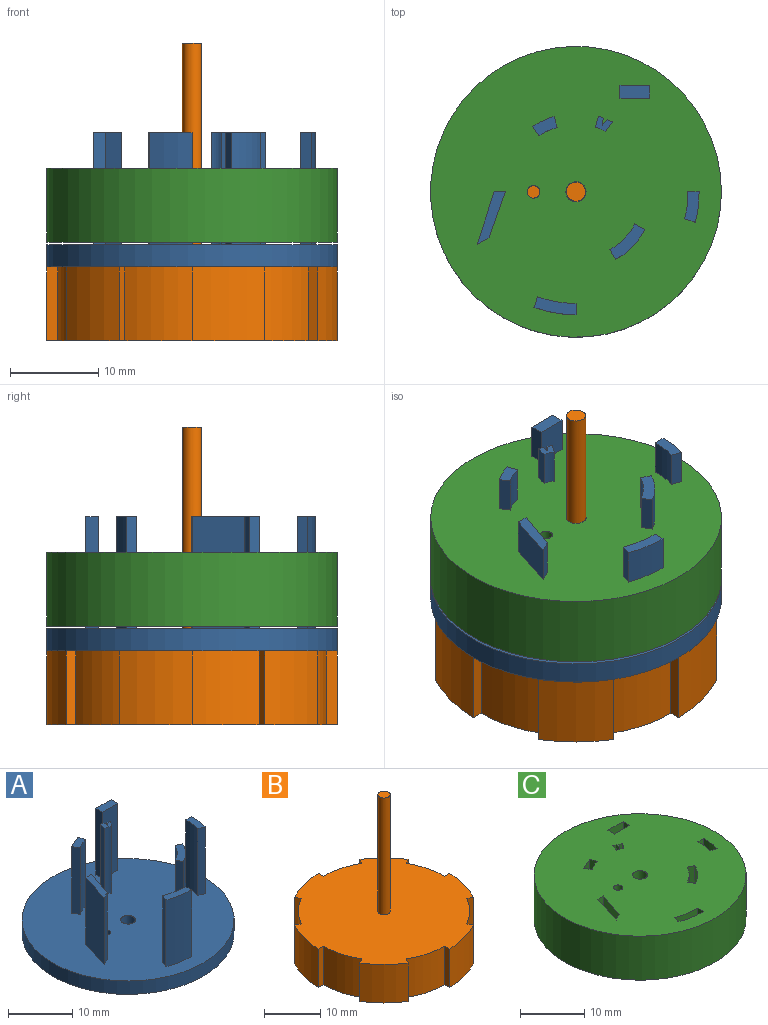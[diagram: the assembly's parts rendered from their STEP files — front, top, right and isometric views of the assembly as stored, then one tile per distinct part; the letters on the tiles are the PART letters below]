
ASSEMBLY  parts=3 mates=2
PART A: 43 faces, bbox 33x33x15.2 mm
  f0: cylinder r=16.51mm len=33.02mm, axis (0,0,-1), area 263.5mm2, adj f3,f4
  f1: cylinder r=0.72mm len=2.54mm, axis (0,0,-1), area 11.4mm2, adj f3,f4
  f2: cylinder r=1.14mm len=2.54mm, axis (0,0,-1), area 18.2mm2, adj f3,f4
  f3: plane 33.02x33.02mm, normal (0,0,1), area 818.2mm2, adj f0,f1,f2,f6,f7,f8,f9,f11
  f4: plane 33.02x33.02mm, normal (0,0,-1), area 850.6mm2, adj f0,f1,f2
  f5: plane 4.78x2.04mm, normal (0,0,1), area 5.9mm2, adj f6,f7,f8,f9
  f6: plane 12.7x1.27mm, normal (1,0,0), area 16.1mm2, adj f3,f5,f7,f9
  f7: cylinder r=14.67mm len=12.7mm, axis (0,0,-1), area 61.9mm2, adj f3,f5,f6,f8
  f8: plane 12.7x1.19mm, normal (-0.94,0.34,0), area 16.1mm2, adj f3,f5,f7,f9
  f9: cylinder r=13.5mm len=12.7mm, axis (0,0,-1), area 56.3mm2, adj f3,f5,f6,f8
  f10: plane 2.82x2.22mm, normal (0,0,1), area 3.2mm2, adj f11,f12,f13,f14
  f11: plane 12.7x1.08mm, normal (-0.83,-0.55,0), area 16.5mm2, adj f3,f10,f12,f14
  f12: cylinder r=10.87mm len=12.7mm, axis (0,0,-1), area 34.5mm2, adj f3,f10,f11,f13
  f13: plane 12.7x1.24mm, normal (0.96,0.28,0), area 16.5mm2, adj f3,f10,f12,f14
  f14: cylinder r=7.47mm len=12.7mm, axis (0,0,-1), area 29.5mm2, adj f3,f10,f11,f13
  f15: plane 4.05x3.98mm, normal (0,0,1), area 5.9mm2, adj f16,f17,f18,f19
  f16: plane 12.7x1.14mm, normal (0.48,0.88,0), area 16.5mm2, adj f3,f15,f17,f19
  f17: cylinder r=7.87mm len=12.7mm, axis (0,0,-1), area 61.6mm2, adj f3,f15,f16,f18
  f18: plane 12.7x1.12mm, normal (-0.86,-0.51,0), area 16.5mm2, adj f3,f15,f17,f19
  f19: cylinder r=6.99mm len=12.7mm, axis (0,0,-1), area 52.6mm2, adj f3,f15,f16,f18
  f20: plane 3.47x1.65mm, normal (0,0,1), area 4.2mm2, adj f21,f22,f23,f24
  f21: plane 12.7x1.27mm, normal (0,1,0), area 16.1mm2, adj f3,f20,f22,f24
  f22: cylinder r=11.39mm len=12.7mm, axis (0,0,-1), area 44.6mm2, adj f3,f20,f21,f23
  f23: plane 12.7x1.21mm, normal (-0.32,-0.95,0), area 16.2mm2, adj f3,f20,f22,f24
  f24: cylinder r=9.62mm len=12.7mm, axis (0,0,-1), area 39.3mm2, adj f3,f20,f21,f23
  f25: plane 5.96x3.21mm, normal (0,0,1), area 6.6mm2, adj f26,f27,f28,f29
  f26: plane 12.7x1.27mm, normal (0,1,0), area 16.1mm2, adj f3,f25,f27,f29
  f27: plane 12.7x5.24mm, normal (0.94,-0.33,0), area 70.6mm2, adj f3,f25,f26,f28
  f28: plane 12.7x1.35mm, normal (0.47,-0.88,0), area 19.4mm2, adj f3,f25,f27,f29
  f29: plane 12.7x5.96mm, normal (-0.95,0.31,0), area 79.5mm2, adj f3,f25,f26,f28
  f30: plane 1.89x1.72mm, normal (0,0,1), area 1.6mm2, adj f31,f32,f33,f34,f35,f36,f37
  f31: plane 12.7x0.85mm, normal (0.99,-0.15,0), area 10.9mm2, adj f3,f30,f32,f37
  f32: plane 12.7x0.68mm, normal (-0.78,0.63,0), area 11.1mm2, adj f3,f30,f31,f33
  f33: plane 12.7x0.57mm, normal (0.43,0.9,0), area 8mm2, adj f3,f30,f32,f34
  f34: plane 12.7x1.06mm, normal (0.81,-0.59,0), area 16.7mm2, adj f3,f30,f33,f35
  f35: cylinder r=2.37mm len=12.7mm, axis (0,0,-1), area 15.4mm2, adj f3,f30,f34,f36
  f36: plane 12.7x1.28mm, normal (-0.97,0.25,0), area 16.8mm2, adj f3,f30,f35,f37
  f37: plane 12.7x0.57mm, normal (0.35,0.94,0), area 7.7mm2, adj f3,f30,f31,f36
  f38: plane 3.35x1.47mm, normal (0,0,1), area 4.9mm2, adj f39,f40,f41,f42
  f39: plane 12.7x1.47mm, normal (1,0,0), area 18.7mm2, adj f3,f38,f40,f42
  f40: plane 12.7x3.35mm, normal (0,-1,0), area 42.6mm2, adj f3,f38,f39,f41
  f41: plane 12.7x1.47mm, normal (-1,0,0), area 18.7mm2, adj f3,f38,f40,f42
  f42: plane 12.7x3.35mm, normal (0,1,0), area 42.6mm2, adj f3,f38,f39,f41
PART B: 28 faces, bbox 33x33x33.8 mm
  f0: cylinder r=15.24mm len=8.38mm, axis (0,0,-1), area 66.9mm2, adj f5,f6,f10,f24
  f1: cylinder r=15.24mm len=8.38mm, axis (0,0,-1), area 66.9mm2, adj f5,f10,f15,f26
  f2: cylinder r=15.24mm len=8.38mm, axis (0,0,-1), area 66.9mm2, adj f5,f10,f14,f18
  f3: cylinder r=15.24mm len=8.38mm, axis (0,0,-1), area 66.9mm2, adj f5,f10,f21,f23
  f4: cylinder r=15.24mm len=8.38mm, axis (0,0,-1), area 66.9mm2, adj f5,f10,f17,f20
  f5: plane 33.02x33.02mm, normal (0,0,1), area 786.3mm2, adj f0,f1,f2,f3,f4,f6,f7,f8
  f6: plane 8.38x1.1mm, normal (-0.87,-0.5,0), area 10.6mm2, adj f0,f5,f9,f10
  f7: cylinder r=15.24mm len=8.38mm, axis (0,0,-1), area 66.9mm2, adj f5,f8,f10,f25
  f8: plane 8.38x1.27mm, normal (1,0,0), area 10.6mm2, adj f5,f7,f9,f10
  f9: cylinder r=19.46mm len=8.38mm, axis (0,0,-1), area 72.2mm2, adj f5,f6,f8,f10
  f10: plane 33.02x33.02mm, normal (0,0,-1), area 790mm2, adj f0,f1,f2,f3,f4,f6,f7,f8
  f11: plane 2.17x2.17mm, normal (0,0,1), area 3.7mm2, adj f12
  f12: cylinder r=1.08mm len=25.4mm, axis (0,0,-1), area 173mm2, adj f5,f11
  f13: cylinder r=19.46mm len=8.38mm, axis (0,0,-1), area 72.2mm2, adj f5,f10,f14,f15
  f14: plane 8.38x1.1mm, normal (-0.5,-0.87,0), area 10.6mm2, adj f2,f5,f10,f13
  f15: plane 8.38x1.27mm, normal (0,1,0), area 10.6mm2, adj f1,f5,f10,f13
  f16: cylinder r=19.46mm len=8.38mm, axis (0,0,-1), area 72.2mm2, adj f5,f10,f17,f18
  f17: plane 8.38x1.27mm, normal (-1,0,0), area 10.6mm2, adj f4,f5,f10,f16
  f18: plane 8.38x1.1mm, normal (0.87,0.5,0), area 10.6mm2, adj f2,f5,f10,f16
  f19: cylinder r=19.46mm len=8.38mm, axis (0,0,-1), area 72.2mm2, adj f5,f10,f20,f21
  f20: plane 8.38x1.1mm, normal (0.87,-0.5,0), area 10.6mm2, adj f4,f5,f10,f19
  f21: plane 8.38x1.1mm, normal (-0.5,0.87,0), area 10.6mm2, adj f3,f5,f10,f19
  f22: cylinder r=19.46mm len=8.38mm, axis (0,0,-1), area 72.2mm2, adj f5,f10,f23,f24
  f23: plane 8.38x1.27mm, normal (0,-1,0), area 10.6mm2, adj f3,f5,f10,f22
  f24: plane 8.38x1.1mm, normal (0.5,0.87,0), area 10.6mm2, adj f0,f5,f10,f22
  f25: plane 8.38x1.1mm, normal (-0.87,0.5,0), area 10.6mm2, adj f5,f7,f10,f27
  f26: plane 8.38x1.1mm, normal (0.5,-0.87,0), area 10.6mm2, adj f1,f5,f10,f27
  f27: cylinder r=19.46mm len=8.38mm, axis (0,0,-1), area 72.2mm2, adj f5,f10,f25,f26
PART C: 36 faces, bbox 33x33x8.4 mm
  f0: plane 8.38x1.19mm, normal (0.94,-0.34,0), area 10.6mm2, adj f1,f33,f34,f35
  f1: cylinder r=13.5mm len=8.38mm, axis (0,0,-1), area 37.1mm2, adj f0,f2,f34,f35
  f2: plane 8.38x1.27mm, normal (-1,0,0), area 10.6mm2, adj f1,f33,f34,f35
  f3: plane 8.38x1.35mm, normal (-0.47,0.88,0), area 12.8mm2, adj f4,f24,f34,f35
  f4: plane 8.38x5.96mm, normal (0.95,-0.31,0), area 52.5mm2, adj f3,f5,f34,f35
  f5: plane 8.38x1.27mm, normal (0,-1,0), area 10.6mm2, adj f4,f24,f34,f35
  f6: plane 8.38x1.24mm, normal (-0.96,-0.28,0), area 10.9mm2, adj f7,f25,f34,f35
  f7: cylinder r=7.47mm len=8.38mm, axis (0,0,-1), area 19.5mm2, adj f6,f8,f34,f35
  f8: plane 8.38x1.08mm, normal (0.83,0.55,0), area 10.9mm2, adj f7,f25,f34,f35
  f9: plane 8.38x1.12mm, normal (0.86,0.51,0), area 10.9mm2, adj f10,f26,f34,f35
  f10: cylinder r=6.99mm len=8.38mm, axis (0,0,-1), area 34.7mm2, adj f9,f11,f34,f35
  f11: plane 8.38x1.14mm, normal (-0.48,-0.88,0), area 10.9mm2, adj f10,f26,f34,f35
  f12: plane 8.38x1.21mm, normal (0.32,0.95,0), area 10.7mm2, adj f13,f27,f34,f35
  f13: cylinder r=9.62mm len=8.38mm, axis (0,0,-1), area 25.9mm2, adj f12,f14,f34,f35
  f14: plane 8.38x1.27mm, normal (0,-1,0), area 10.6mm2, adj f13,f27,f34,f35
  f15: plane 8.38x1.28mm, normal (0.97,-0.25,0), area 11.1mm2, adj f16,f31,f34,f35
  f16: plane 8.38x0.57mm, normal (-0.35,-0.94,0), area 5.1mm2, adj f15,f17,f34,f35
  f17: plane 8.38x0.85mm, normal (-0.99,0.15,0), area 7.2mm2, adj f16,f18,f34,f35
  f18: plane 8.38x0.68mm, normal (0.78,-0.63,0), area 7.3mm2, adj f17,f19,f34,f35
  f19: plane 8.38x0.57mm, normal (-0.43,-0.9,0), area 5.3mm2, adj f18,f20,f34,f35
  f20: plane 8.38x1.06mm, normal (-0.81,0.59,0), area 11mm2, adj f19,f31,f34,f35
  f21: plane 8.38x1.47mm, normal (1,0,0), area 12.3mm2, adj f22,f32,f34,f35
  f22: plane 8.38x3.35mm, normal (0,-1,0), area 28.1mm2, adj f21,f23,f34,f35
  f23: plane 8.38x1.47mm, normal (-1,0,0), area 12.3mm2, adj f22,f32,f34,f35
  f24: plane 8.38x5.24mm, normal (-0.94,0.33,0), area 46.6mm2, adj f3,f5,f34,f35
  f25: cylinder r=10.87mm len=8.38mm, axis (0,0,-1), area 22.8mm2, adj f6,f8,f34,f35
  f26: cylinder r=7.87mm len=8.38mm, axis (0,0,-1), area 40.6mm2, adj f9,f11,f34,f35
  f27: cylinder r=11.39mm len=8.38mm, axis (0,0,-1), area 29.4mm2, adj f12,f14,f34,f35
  f28: cylinder r=16.51mm len=33.02mm, axis (0,0,-1), area 869.5mm2, adj f34,f35
  f29: cylinder r=0.72mm len=8.38mm, axis (0,0,-1), area 37.7mm2, adj f34,f35
  f30: cylinder r=1.14mm len=8.38mm, axis (0,0,-1), area 60.2mm2, adj f34,f35
  f31: cylinder r=2.37mm len=8.38mm, axis (0,0,-1), area 10.2mm2, adj f15,f20,f34,f35
  f32: plane 8.38x3.35mm, normal (0,1,0), area 28.1mm2, adj f21,f23,f34,f35
  f33: cylinder r=14.67mm len=8.38mm, axis (0,0,-1), area 40.9mm2, adj f0,f2,f34,f35
  f34: plane 33.02x33.02mm, normal (0,0,1), area 818.2mm2, adj f0,f1,f2,f3,f4,f5,f6,f7
  f35: plane 33.02x33.02mm, normal (0,0,-1), area 818.2mm2, adj f0,f1,f2,f3,f4,f5,f6,f7
PLACE A t=(62.65,-5.43,-1.46)mm
PLACE B t=(62.65,-5.43,-9.84)mm
PLACE C t=(62.65,-5.43,1.36)mm
MATE slider C.f30 <-> B.f12  axis (0,0,1) through (62.65,-5.43,9.74)mm
MATE cylindrical A.f2 <-> B.f12  axis (0,0,-1) through (62.65,-5.43,-1.46)mm
